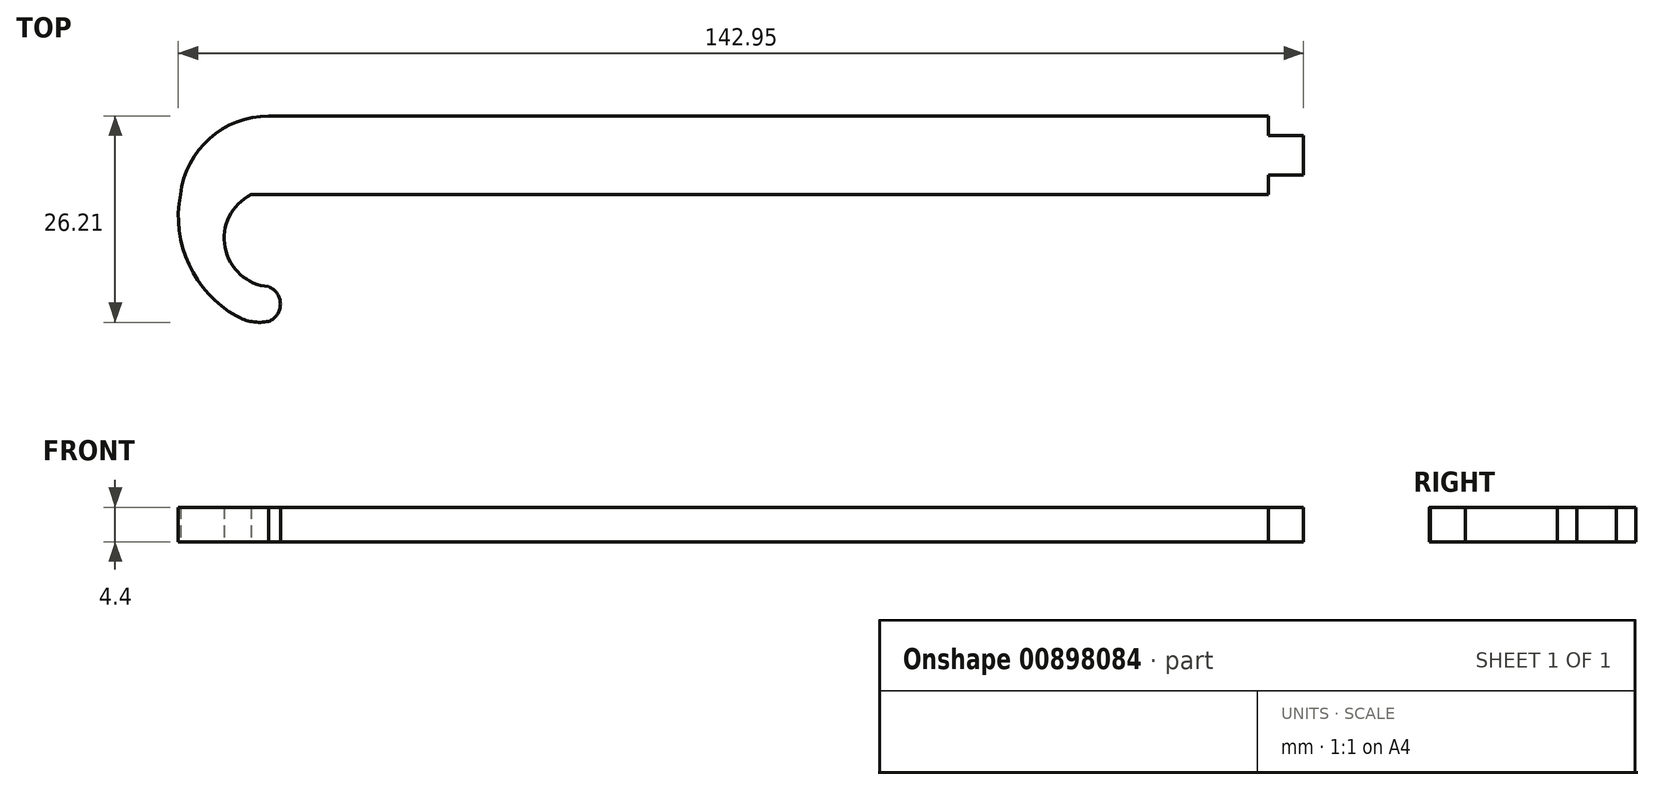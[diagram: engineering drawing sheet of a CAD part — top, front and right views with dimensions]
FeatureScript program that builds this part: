
annotation { "Feature Type Name" : "Feature", "Feature Type Description" : "" }
export const myFeature = defineFeature(function(context is Context, id is Id, definition is map)
    precondition{}
    {
        {
            var Q0;
            Q0=qCreatedBy(makeId("Top.planeOp"),FACE);
            var sketch = newSketch(context, id + "F0", { "sketchPlane" : qUnion([Q0])});
            skLineSegment(sketch, "E0", {"start": v(0, 18.7) * mm, "end": v(-127, 18.7) * mm});
            skArc(sketch, "E1", {"start": v(-127, 18.7) * mm, "mid": v(-134.52, 15.84) * mm, "end": v(-138.23, 8.7) * mm});
            skLineSegment(sketch, "E2", {"start": v(-122.6, 8.7) * mm, "end": v(0, 8.7) * mm});
            skLineSegment(sketch, "E3", {"start": v(0, 8.7) * mm, "end": v(0, 11.2) * mm});
            skArc(sketch, "E4", {"start": v(-127, -7.4) * mm, "mid": v(-125.53, -5.2) * mm, "end": v(-127, -3) * mm});
            skArc(sketch, "E5", {"start": v(-138.23, 8.7) * mm, "mid": v(-137.15, -0.17) * mm, "end": v(-131.08, -6.73) * mm});
            skArc(sketch, "E6", {"start": v(-131.08, -6.73) * mm, "mid": v(-129.1, -7.43) * mm, "end": v(-127, -7.4) * mm});
            skArc(sketch, "E7", {"start": v(-129.24, 8.7) * mm, "mid": v(-132.56, 2) * mm, "end": v(-127, -3) * mm});
            skLineSegment(sketch, "E8", {"start": v(-129.24, 8.7) * mm, "end": v(-122.6, 8.7) * mm});
            skLineSegment(sketch, "E9", {"start": v(0, 16.2) * mm, "end": v(4.45, 16.2) * mm});
            skLineSegment(sketch, "E10", {"start": v(4.45, 16.2) * mm, "end": v(4.45, 11.2) * mm});
            skLineSegment(sketch, "E11", {"start": v(4.45, 11.2) * mm, "end": v(0, 11.2) * mm});
            skLineSegment(sketch, "E12.trimOffspring", {"start": v(0, 16.2) * mm, "end": v(0, 18.7) * mm});
            skSolve(sketch);
        }
        {
            var Q0;
            Q0 = qSketchRegion(id + "F0", true);
            extrude(context, id + "F1", {"entities" : qUnion([Q0]), "depth" : 4.4 * mm, "offsetDistance" : 25 * mm});
        }
    });
